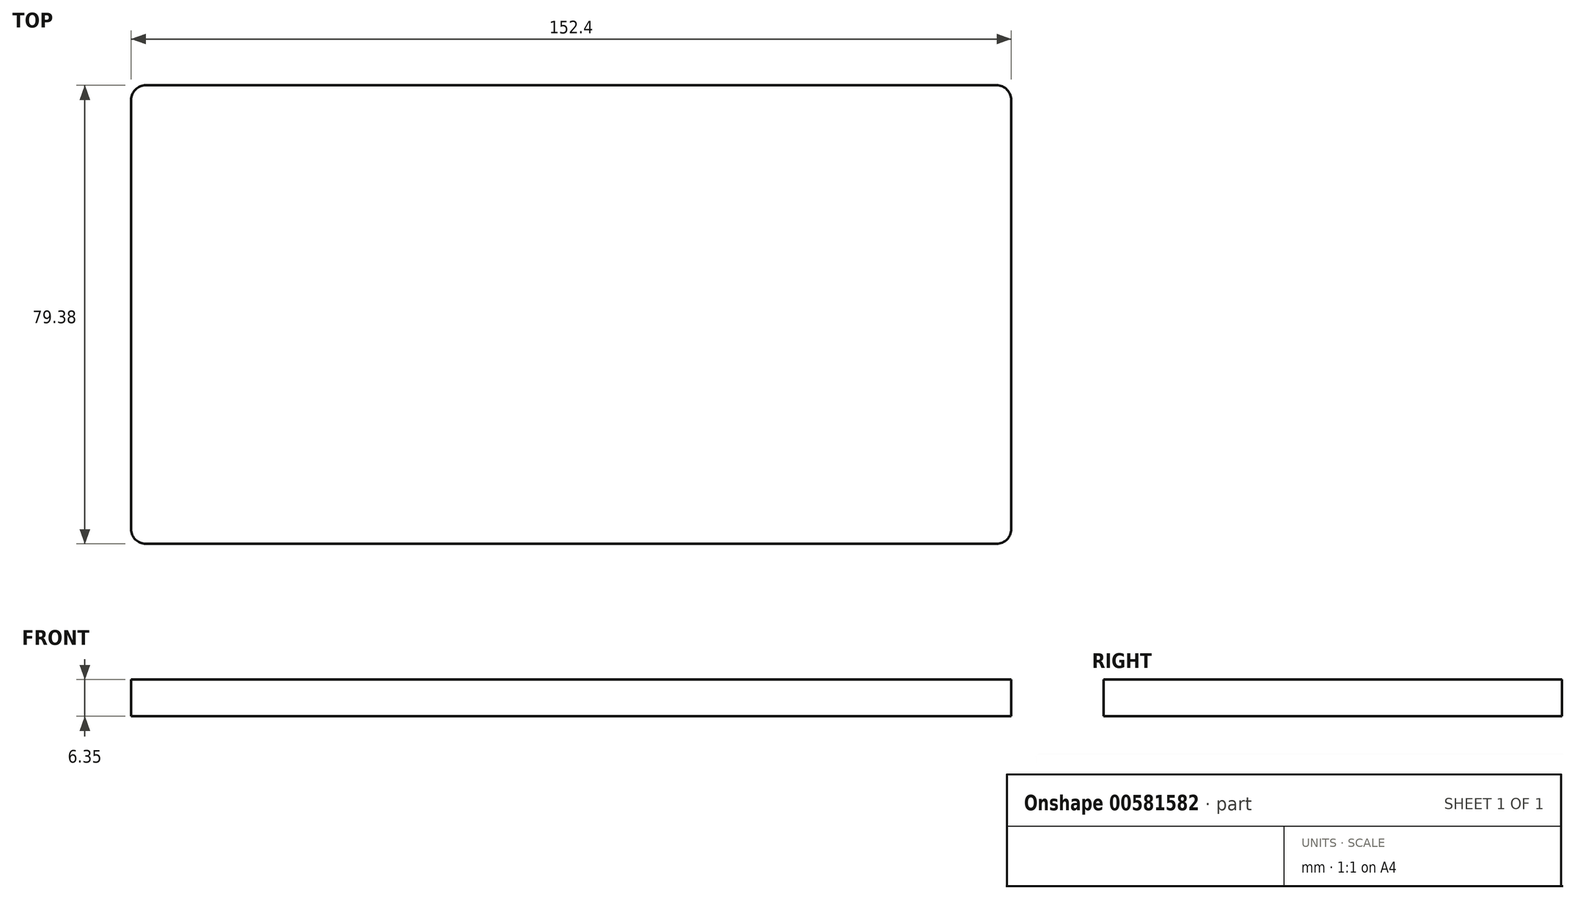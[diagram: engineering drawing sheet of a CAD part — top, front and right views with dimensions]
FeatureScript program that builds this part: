
annotation { "Feature Type Name" : "Feature", "Feature Type Description" : "" }
export const myFeature = defineFeature(function(context is Context, id is Id, definition is map)
    precondition{}
    {
        {
            var Q0;
            Q0=qCreatedBy(makeId("Top.planeOp"),FACE);
            var sketch = newSketch(context, id + "F0", { "sketchPlane" : qUnion([Q0])});
            skLineSegment(sketch, "E0.bottom", {"start": v(-76.2, 39.69) * mm, "end": v(76.2, 39.69) * mm});
            skLineSegment(sketch, "E0.top", {"start": v(-76.2, -39.69) * mm, "end": v(76.2, -39.69) * mm});
            skLineSegment(sketch, "E0.left", {"start": v(-76.2, 39.69) * mm, "end": v(-76.2, -39.69) * mm});
            skLineSegment(sketch, "E0.right", {"start": v(76.2, 39.69) * mm, "end": v(76.2, -39.69) * mm});
            skPoint(sketch, "E0.middle", {"position": v(0, 0) * mm});
            skSolve(sketch);
        }
        {
            var Q0;
            Q0=makeQuery(id+"F0.imprint","IMPRINT",FACE,{"disambiguationData":[TD([[makeQuery(id+"F0.imprint","IMPRINT",EDGE,{"derivedFrom":sQuery(id+"F0.wireOp",EDGE,"E0.bottom")}),-1.0]])]});
            extrude(context, id + "F1", {"entities" : qUnion([Q0]), "depth" : 6.35 * mm, "offsetDistance" : 25.4 * mm});
        }
        {
            var Q0;
            Q0=makeQuery(id+"F1.opExtrude","SWEPT_EDGE",EDGE,{"disambiguationData":[OSD([sQuery(id+"F0.wireOp",EDGE,"E0.top"),sQuery(id+"F0.wireOp",EDGE,"E0.left")])]});
            var Q1;
            Q1=makeQuery(id+"F1.opExtrude","SWEPT_EDGE",EDGE,{"disambiguationData":[OSD([sQuery(id+"F0.wireOp",EDGE,"E0.bottom"),sQuery(id+"F0.wireOp",EDGE,"E0.left")])]});
            var Q2;
            Q2=makeQuery(id+"F1.opExtrude","SWEPT_EDGE",EDGE,{"disambiguationData":[OSD([sQuery(id+"F0.wireOp",EDGE,"E0.top"),sQuery(id+"F0.wireOp",EDGE,"E0.right")])]});
            var Q3;
            Q3=makeQuery(id+"F1.opExtrude","SWEPT_EDGE",EDGE,{"disambiguationData":[OSD([sQuery(id+"F0.wireOp",EDGE,"E0.bottom"),sQuery(id+"F0.wireOp",EDGE,"E0.right")])]});
            fillet(context, id + "F2", {"entities" : qUnion([Q0, Q1, Q2, Q3]), "radius" : 2.54 * mm, "tangentPropagation" : true, "allowEdgeOverflow" : false});
        }
    });
